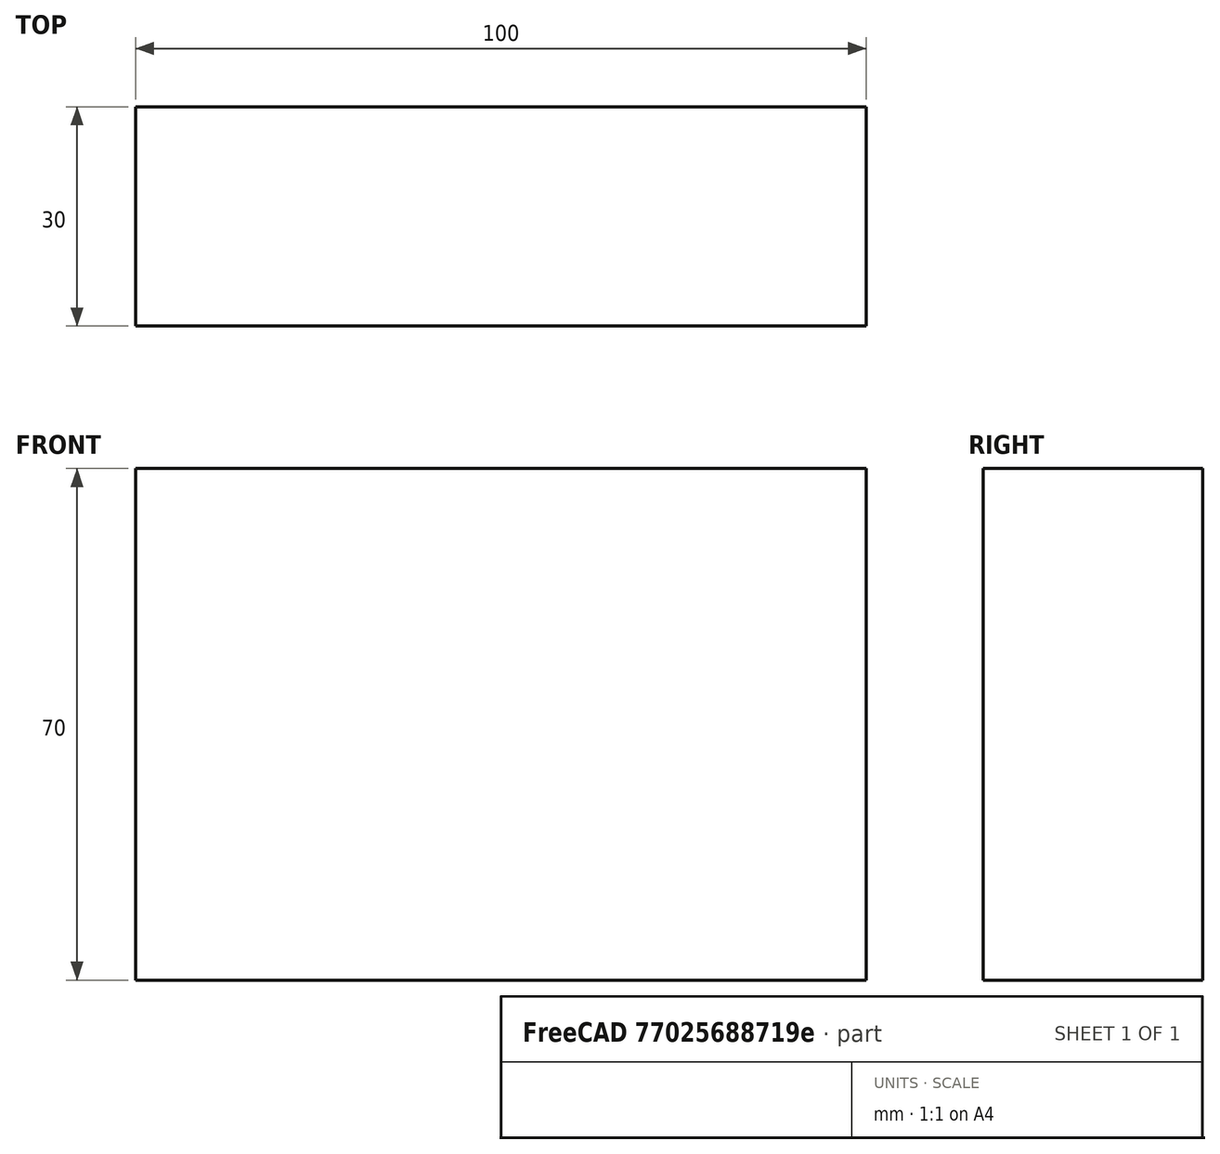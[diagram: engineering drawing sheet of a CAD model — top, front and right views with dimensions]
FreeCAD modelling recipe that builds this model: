
FCSTD DOCUMENT  (FreeCAD 0.19R24276 (Git))
Label: brus_100x70x30
License: All rights reserved
LicenseURL: http://en.wikipedia.org/wiki/All_rights_reserved
objects: Sketcher::SketchObject×1, PartDesign::Pad×1, PartDesign::Body×1
note: 4 computed .brp shape members not serialized (recipe doc carries the construction recipe); baked Part::Feature solids carry a one-line shape summary decoded from their .brp

FEATURE [Sketcher::SketchObject] Sketch
  FullyConstrained = true
  MapMode = 5
  Support = -> [XY_Plane]
  sketch-geometry (4):
    g0: LineSegment StartX=0 StartY=0 StartZ=0 EndX=100 EndY=0 EndZ=0
    g1: LineSegment StartX=100 StartY=0 StartZ=0 EndX=100 EndY=30 EndZ=0
    g2: LineSegment StartX=100 StartY=30 StartZ=0 EndX=0 EndY=30 EndZ=0
    g3: LineSegment StartX=0 StartY=30 StartZ=0 EndX=0 EndY=0 EndZ=0
  constraints (11):
    c: Coincident(g0,g1)
    c: Coincident(g1,g2)
    c: Coincident(g2,g3)
    c: Coincident(g3,g0)
    c: Horizontal(g0)
    c: Horizontal(g2)
    c: Vertical(g1)
    c: Vertical(g3)
    c: Coincident(g0,g-1)
    c: DistanceX(g0,g0) = 100
    c: DistanceY(g3,g3) = 30
FEATURE [PartDesign::Pad] Pad
  Direction = (1,1,1)
  Length = 70
  Length2 = 100
  Profile = -> Sketch
  Type = 0
FEATURE [PartDesign::Body] Body
  Group = -> [Sketch,Pad]
  Origin = -> Origin
  Tip = -> Pad
